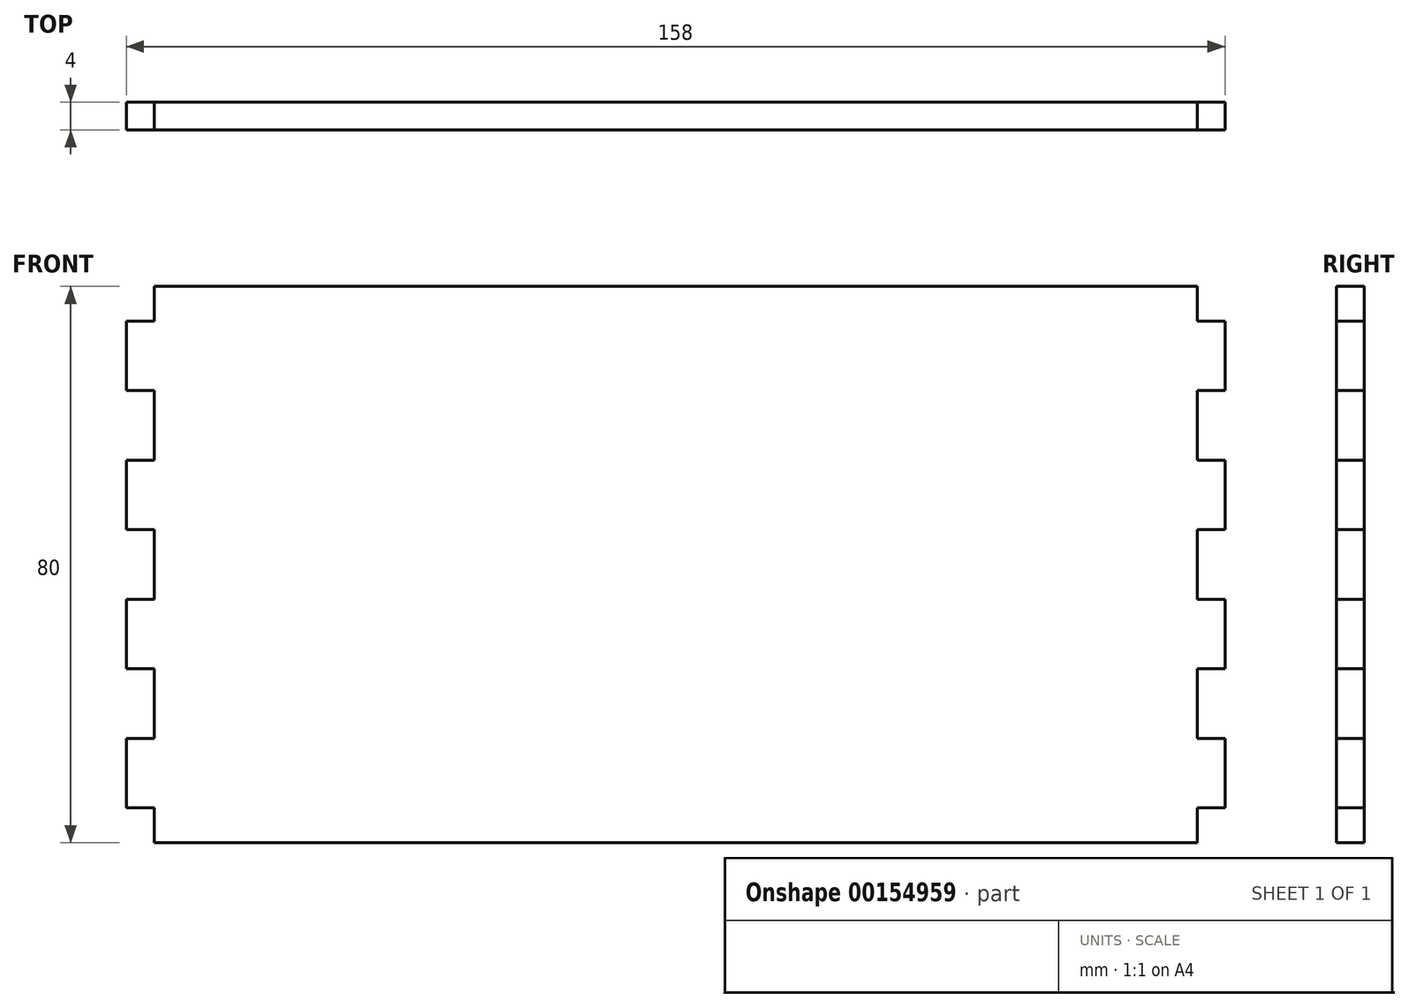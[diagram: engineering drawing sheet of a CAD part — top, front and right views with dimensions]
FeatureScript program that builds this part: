
annotation { "Feature Type Name" : "Feature", "Feature Type Description" : "" }
export const myFeature = defineFeature(function(context is Context, id is Id, definition is map)
    precondition{}
    {
        {
            var Q0;
            Q0=qCreatedBy(makeId("Front.planeOp"),FACE);
            var sketch = newSketch(context, id + "F0", { "sketchPlane" : qUnion([Q0])});
            skLineSegment(sketch, "E0.bottom", {"start": v(75, 38.7) * mm, "end": v(-75, 38.7) * mm});
            skLineSegment(sketch, "E0.top", {"start": v(75, -41.3) * mm, "end": v(-75, -41.3) * mm});
            skLineSegment(sketch, "E0.left", {"start": v(75, 38.7) * mm, "end": v(75, -41.3) * mm});
            skLineSegment(sketch, "E0.right", {"start": v(-75, 38.7) * mm, "end": v(-75, -41.3) * mm});
            skPoint(sketch, "E0.middle", {"position": v(0, -1.3) * mm});
            skSolve(sketch);
        }
        {
            var Q0;
            Q0=makeQuery(id+"F0.imprint","IMPRINT",FACE,{"disambiguationData":[TD([[makeQuery(id+"F0.imprint","IMPRINT",EDGE,{"derivedFrom":sQuery(id+"F0.wireOp",EDGE,"E0.bottom")}),1.0]])]});
            extrude(context, id + "F1", {"entities" : qUnion([Q0]), "depth" : 4 * mm});
        }
        {
            var Q0;
            Q0=makeQuery(id+"F1.opExtrude","CAP_FACE",FACE,{"disambiguationData":[OSD([sQuery(id+"F0.wireOp",EDGE,"E0.bottom"),sQuery(id+"F0.wireOp",EDGE,"E0.top"),sQuery(id+"F0.wireOp",EDGE,"E0.left"),sQuery(id+"F0.wireOp",EDGE,"E0.right")])],"isStart":false});
            var sketch = newSketch(context, id + "F2", { "sketchPlane" : qUnion([Q0])});
            skLineSegment(sketch, "E1", {"start": v(-75, 38.7) * mm, "end": v(-75, 33.7) * mm});
            skLineSegment(sketch, "E2", {"start": v(-75, 33.7) * mm, "end": v(-79, 33.7) * mm});
            skLineSegment(sketch, "E3", {"start": v(-79, 33.7) * mm, "end": v(-79, 23.7) * mm});
            skLineSegment(sketch, "E4", {"start": v(-79, 23.7) * mm, "end": v(-75, 23.7) * mm});
            skLineSegment(sketch, "E5", {"start": v(-75, 23.7) * mm, "end": v(-75, 33.7) * mm});
            skLineSegment(sketch, "E6.0.1.0", {"start": v(-75, 3.7) * mm, "end": v(-75, 13.7) * mm});
            skLineSegment(sketch, "E6.0.1.1", {"start": v(-79, 3.7) * mm, "end": v(-75, 3.7) * mm});
            skLineSegment(sketch, "E6.0.1.2", {"start": v(-79, 13.7) * mm, "end": v(-79, 3.7) * mm});
            skLineSegment(sketch, "E6.0.1.3", {"start": v(-75, 13.7) * mm, "end": v(-79, 13.7) * mm});
            skLineSegment(sketch, "E6.0.2.0", {"start": v(-75, -16.3) * mm, "end": v(-75, -6.3) * mm});
            skLineSegment(sketch, "E6.0.2.1", {"start": v(-79, -16.3) * mm, "end": v(-75, -16.3) * mm});
            skLineSegment(sketch, "E6.0.2.2", {"start": v(-79, -6.3) * mm, "end": v(-79, -16.3) * mm});
            skLineSegment(sketch, "E6.0.2.3", {"start": v(-75, -6.3) * mm, "end": v(-79, -6.3) * mm});
            skLineSegment(sketch, "E6.0.3.0", {"start": v(-75, -36.3) * mm, "end": v(-75, -26.3) * mm});
            skLineSegment(sketch, "E6.0.3.1", {"start": v(-79, -36.3) * mm, "end": v(-75, -36.3) * mm});
            skLineSegment(sketch, "E6.0.3.2", {"start": v(-79, -26.3) * mm, "end": v(-79, -36.3) * mm});
            skLineSegment(sketch, "E6.0.3.3", {"start": v(-75, -26.3) * mm, "end": v(-79, -26.3) * mm});
            skLineSegment(sketch, "E6.direction1", {"start": v(-79, 23.7) * mm, "end": v(-54, 23.7) * mm, "construction": true});
            skLineSegment(sketch, "E6.direction2", {"start": v(-79, 23.7) * mm, "end": v(-79, 3.7) * mm, "construction": true});
            skLineSegment(sketch, "E7", {"start": v(0, 38.7) * mm, "end": v(0, 31.03) * mm});
            skPoint(sketch, "E7.endSnap0", {"position": v(0, 38.7) * mm});
            skLineSegment(sketch, "E8.MirrorCS", {"start": v(75, 38.7) * mm, "end": v(75, 33.7) * mm});
            skLineSegment(sketch, "E9.MirrorCS", {"start": v(79, 13.7) * mm, "end": v(79, 3.7) * mm});
            skLineSegment(sketch, "E10.MirrorCS", {"start": v(79, 23.7) * mm, "end": v(75, 23.7) * mm});
            skLineSegment(sketch, "E11.MirrorCS", {"start": v(79, 3.7) * mm, "end": v(75, 3.7) * mm});
            skLineSegment(sketch, "E12.MirrorCS", {"start": v(75, 3.7) * mm, "end": v(75, 13.7) * mm});
            skLineSegment(sketch, "E13.MirrorCS", {"start": v(75, 13.7) * mm, "end": v(79, 13.7) * mm});
            skLineSegment(sketch, "E14.MirrorCS", {"start": v(75, -16.3) * mm, "end": v(75, -6.3) * mm});
            skLineSegment(sketch, "E15.MirrorCS", {"start": v(79, -16.3) * mm, "end": v(75, -16.3) * mm});
            skLineSegment(sketch, "E16.MirrorCS", {"start": v(79, -6.3) * mm, "end": v(79, -16.3) * mm});
            skLineSegment(sketch, "E17.MirrorCS", {"start": v(75, -6.3) * mm, "end": v(79, -6.3) * mm});
            skLineSegment(sketch, "E18.MirrorCS", {"start": v(79, -26.3) * mm, "end": v(79, -36.3) * mm});
            skLineSegment(sketch, "E19.MirrorCS", {"start": v(79, -36.3) * mm, "end": v(75, -36.3) * mm});
            skLineSegment(sketch, "E20.MirrorCS", {"start": v(75, 23.7) * mm, "end": v(75, 33.7) * mm});
            skLineSegment(sketch, "E21.MirrorCS", {"start": v(79, 33.7) * mm, "end": v(79, 23.7) * mm});
            skLineSegment(sketch, "E22.MirrorCS", {"start": v(79, 23.7) * mm, "end": v(79, 3.7) * mm, "construction": true});
            skLineSegment(sketch, "E23.MirrorCS", {"start": v(75, -26.3) * mm, "end": v(79, -26.3) * mm});
            skLineSegment(sketch, "E24.MirrorCS", {"start": v(75, -36.3) * mm, "end": v(75, -26.3) * mm});
            skLineSegment(sketch, "E25.MirrorCS", {"start": v(75, 33.7) * mm, "end": v(79, 33.7) * mm});
            skLineSegment(sketch, "E26.MirrorCS", {"start": v(79, 23.7) * mm, "end": v(54, 23.7) * mm, "construction": true});
            skSolve(sketch);
        }
        {
            var Q0;
            Q0 = qSketchRegion(id + "F2", true);
            extrude(context, id + "F3", {"entities" : qUnion([Q0]), "operationType" : NewBodyOperationType.ADD, "oppositeDirection" : true, "depth" : 4 * mm});
        }
    });
